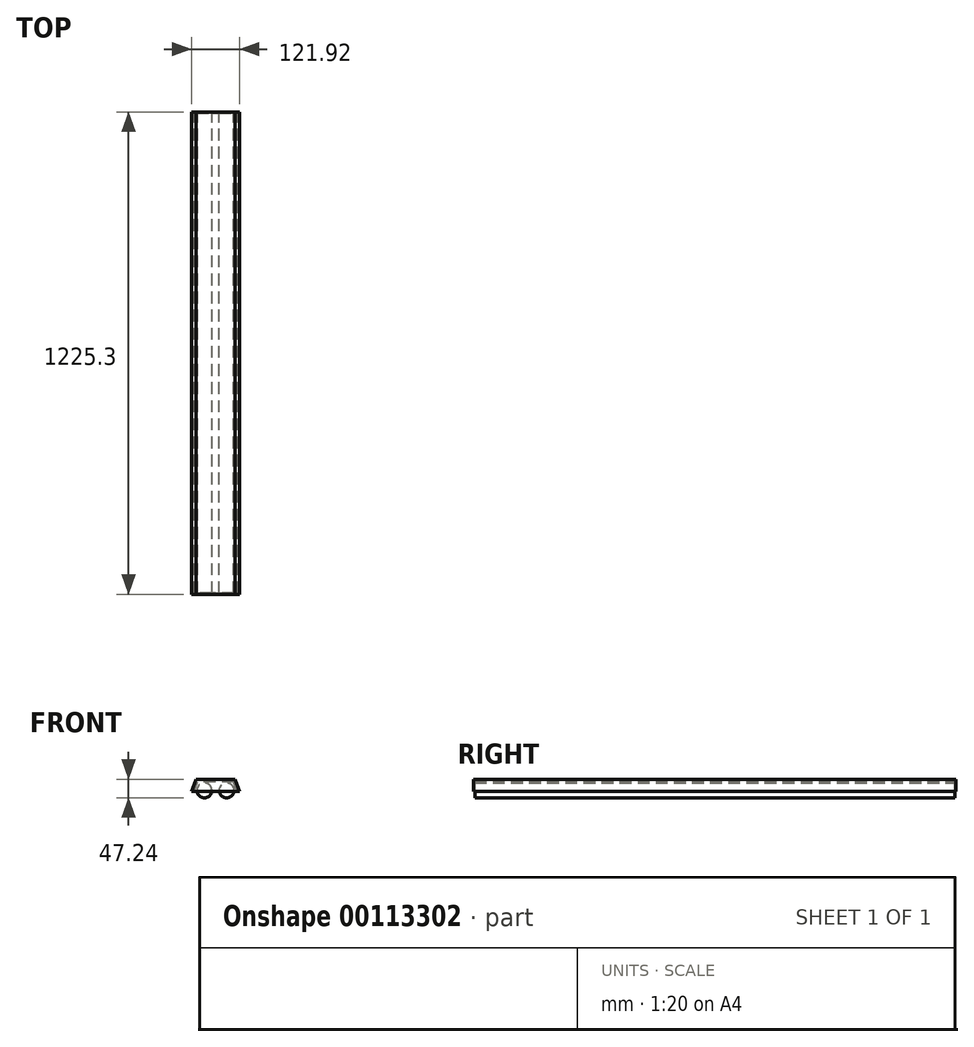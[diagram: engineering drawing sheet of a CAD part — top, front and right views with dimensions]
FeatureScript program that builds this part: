
annotation { "Feature Type Name" : "Feature", "Feature Type Description" : "" }
export const myFeature = defineFeature(function(context is Context, id is Id, definition is map)
    precondition{}
    {
        {
            var Q0;
            Q0=qCreatedBy(makeId("Front.planeOp"),FACE);
            var sketch = newSketch(context, id + "F0", { "sketchPlane" : qUnion([Q0])});
            skLineSegment(sketch, "E0", {"start": v(0, 0) * mm, "end": v(49.87, 0) * mm});
            skLineSegment(sketch, "E1", {"start": v(49.87, 0) * mm, "end": v(60.96, -30.48) * mm});
            skLineSegment(sketch, "E2", {"start": v(60.96, -30.48) * mm, "end": v(54.86, -30.48) * mm});
            skLineSegment(sketch, "E3", {"start": v(54.86, -30.48) * mm, "end": v(45.99, -6.1) * mm});
            skLineSegment(sketch, "E4", {"start": v(45.99, -6.1) * mm, "end": v(0, -6.1) * mm});
            skLineSegment(sketch, "E5", {"start": v(0, -6.1) * mm, "end": v(0, 0) * mm});
            skCircle(sketch, "E6", {"center": v(28.2, -28.2) * mm, "radius": 19.05 * mm});
            skSolve(sketch);
        }
        {
            var Q0;
            Q0 = qSketchRegion(id + "F0", true);
            extrude(context, id + "F1", {"entities" : qUnion([Q0]), "depth" : 1219.2 * mm, "symmetric" : true});
        }
        {
            var Q0;
            Q0=makeQuery(id+"F1.opExtrude","SWEPT_BODY",BODY,{"disambiguationData":[OSD([sQuery(id+"F0.wireOp",EDGE,"E6")])]});
            var Q1;
            Q1=makeQuery(id+"F1.opExtrude","SWEPT_BODY",BODY,{"disambiguationData":[OSD([sQuery(id+"F0.wireOp",EDGE,"E0"),sQuery(id+"F0.wireOp",EDGE,"E1"),sQuery(id+"F0.wireOp",EDGE,"E2"),sQuery(id+"F0.wireOp",EDGE,"E3"),sQuery(id+"F0.wireOp",EDGE,"E4"),sQuery(id+"F0.wireOp",EDGE,"E5")])]});
            var Q2;
            Q2=qCreatedBy(makeId("Right.planeOp"),FACE);
            mirror(context, id + "F2", {"operationType" : NewBodyOperationType.ADD, "entities" : qUnion([Q0, Q1]), "mirrorPlane" : qUnion([Q2])});
        }
        {
            var Q0;
            {var subQ0=makeQuery(id+"F1.opExtrude","CAP_FACE",FACE,{"disambiguationData":[OSD([sQuery(id+"F0.wireOp",EDGE,"E0"),sQuery(id+"F0.wireOp",EDGE,"E1"),sQuery(id+"F0.wireOp",EDGE,"E2"),sQuery(id+"F0.wireOp",EDGE,"E3"),sQuery(id+"F0.wireOp",EDGE,"E4"),sQuery(id+"F0.wireOp",EDGE,"E5")])],"isStart":false});Q0=makeQuery(id+"F2.boolean.opBoolean","MERGE",FACE,{"derivedFrom":[subQ0,makeQuery(id+"F2.opPattern","COPY",FACE,{"derivedFrom":subQ0,"instanceName":"1"})]});}
            var sketch = newSketch(context, id + "F3", { "sketchPlane" : qUnion([Q0])});
            skLineSegment(sketch, "E7.0", {"start": v(-49.87, 0) * mm, "end": v(-60.96, -30.48) * mm});
            skLineSegment(sketch, "E7.1", {"start": v(-49.87, 0) * mm, "end": v(49.87, 0) * mm});
            skLineSegment(sketch, "E7.2", {"start": v(49.87, 0) * mm, "end": v(60.96, -30.48) * mm});
            skLineSegment(sketch, "E8", {"start": v(-60.96, -30.48) * mm, "end": v(60.96, -30.48) * mm});
            skSolve(sketch);
        }
        {
            var Q0;
            Q0 = qSketchRegion(id + "F3", true);
            extrude(context, id + "F4", {"entities" : qUnion([Q0]), "depth" : 3.05 * mm});
        }
        {
            var Q0;
            Q0=makeQuery(id+"F4.opExtrude","SWEPT_BODY",BODY,{"disambiguationData":[OSD([sQuery(id+"F3.wireOp",EDGE,"E7.0"),sQuery(id+"F3.wireOp",EDGE,"E7.1"),sQuery(id+"F3.wireOp",EDGE,"E7.2"),sQuery(id+"F3.wireOp",EDGE,"E8")])]});
            var Q1;
            Q1=qCreatedBy(makeId("Front.planeOp"),FACE);
            mirror(context, id + "F5", {"operationType" : NewBodyOperationType.ADD, "entities" : qUnion([Q0]), "mirrorPlane" : qUnion([Q1])});
        }
    });
